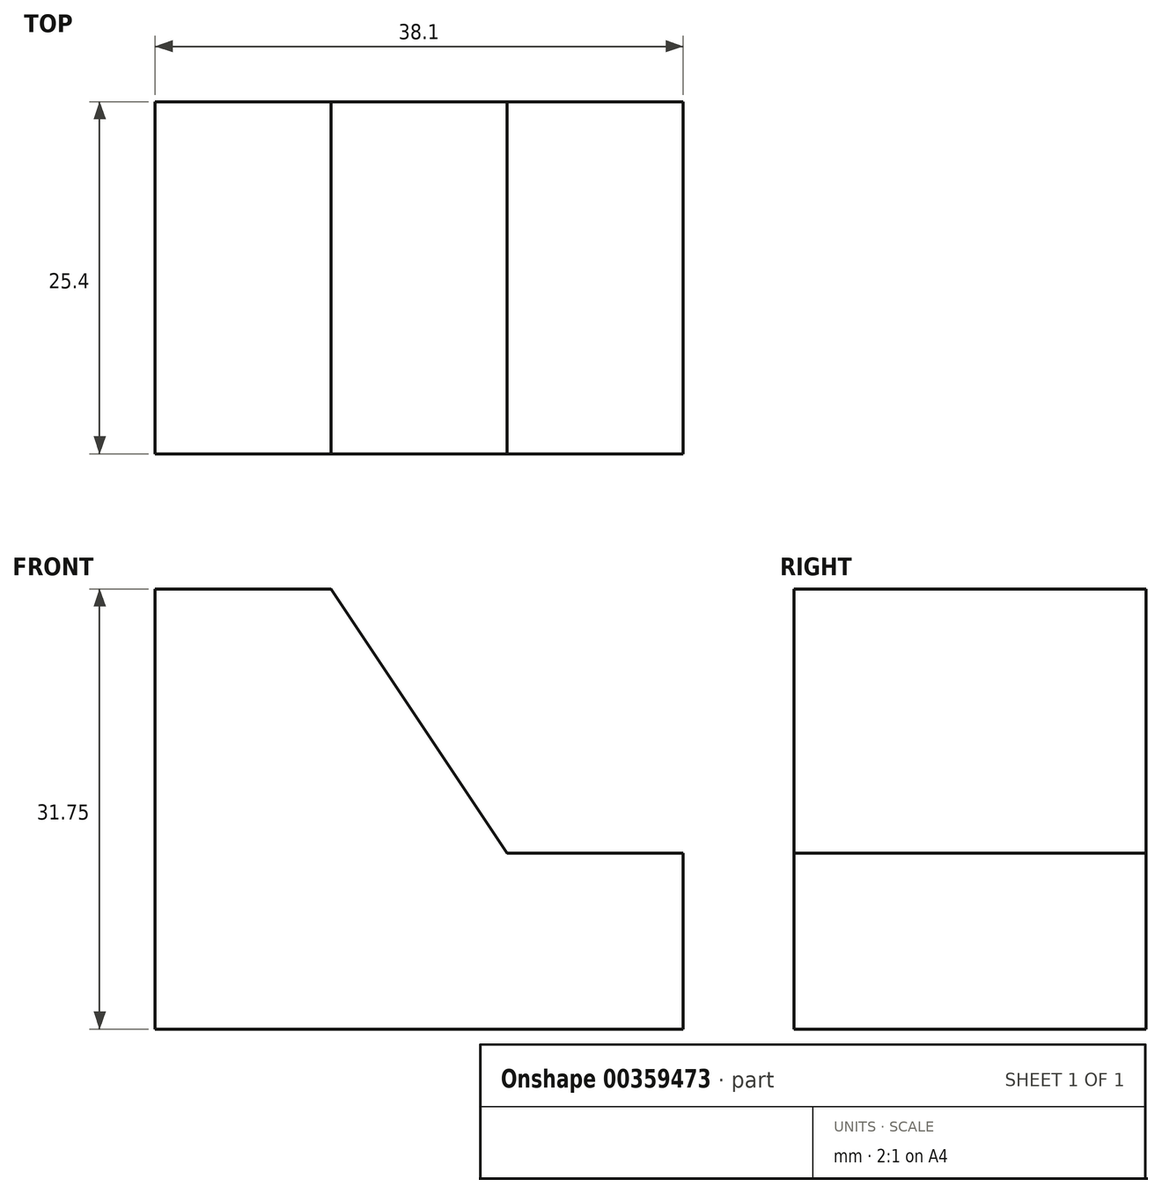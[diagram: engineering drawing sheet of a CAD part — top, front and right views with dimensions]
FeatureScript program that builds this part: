
annotation { "Feature Type Name" : "Feature", "Feature Type Description" : "" }
export const myFeature = defineFeature(function(context is Context, id is Id, definition is map)
    precondition{}
    {
        {
            var Q0;
            Q0=qCreatedBy(makeId("Front.planeOp"),FACE);
            var sketch = newSketch(context, id + "F0", { "sketchPlane" : qUnion([Q0])});
            skLineSegment(sketch, "E0", {"start": v(12.21, 38.67) * mm, "end": v(12.21, 6.92) * mm});
            skLineSegment(sketch, "E1", {"start": v(12.21, 6.92) * mm, "end": v(50.31, 6.92) * mm});
            skLineSegment(sketch, "E2", {"start": v(50.31, 6.92) * mm, "end": v(50.31, 38.67) * mm});
            skLineSegment(sketch, "E3", {"start": v(50.31, 38.67) * mm, "end": v(12.21, 38.67) * mm});
            skSolve(sketch);
        }
        {
            var Q0;
            Q0=makeQuery(id+"F0.imprint","IMPRINT",FACE,{"disambiguationData":[TD([[makeQuery(id+"F0.imprint","IMPRINT",EDGE,{"derivedFrom":sQuery(id+"F0.wireOp",EDGE,"E0")}),1.0]])]});
            extrude(context, id + "F1", {"entities" : qUnion([Q0]), "depth" : 25.4 * mm});
        }
        {
            var Q0;
            Q0=qCreatedBy(makeId("Front.planeOp"),FACE);
            var sketch = newSketch(context, id + "F2", { "sketchPlane" : qUnion([Q0])});
            skLineSegment(sketch, "E4", {"start": v(24.91, 38.67) * mm, "end": v(37.61, 19.62) * mm});
            skLineSegment(sketch, "E5", {"start": v(37.61, 19.62) * mm, "end": v(50.31, 19.62) * mm});
            skLineSegment(sketch, "E6", {"start": v(50.31, 19.62) * mm, "end": v(50.31, 38.67) * mm});
            skLineSegment(sketch, "E7", {"start": v(50.31, 38.67) * mm, "end": v(24.91, 38.67) * mm});
            skSolve(sketch);
        }
        {
            var Q0;
            Q0 = qSketchRegion(id + "F2", true);
            extrude(context, id + "F3", {"entities" : qUnion([Q0]), "operationType" : NewBodyOperationType.REMOVE, "depth" : 25.4 * mm});
        }
    });
